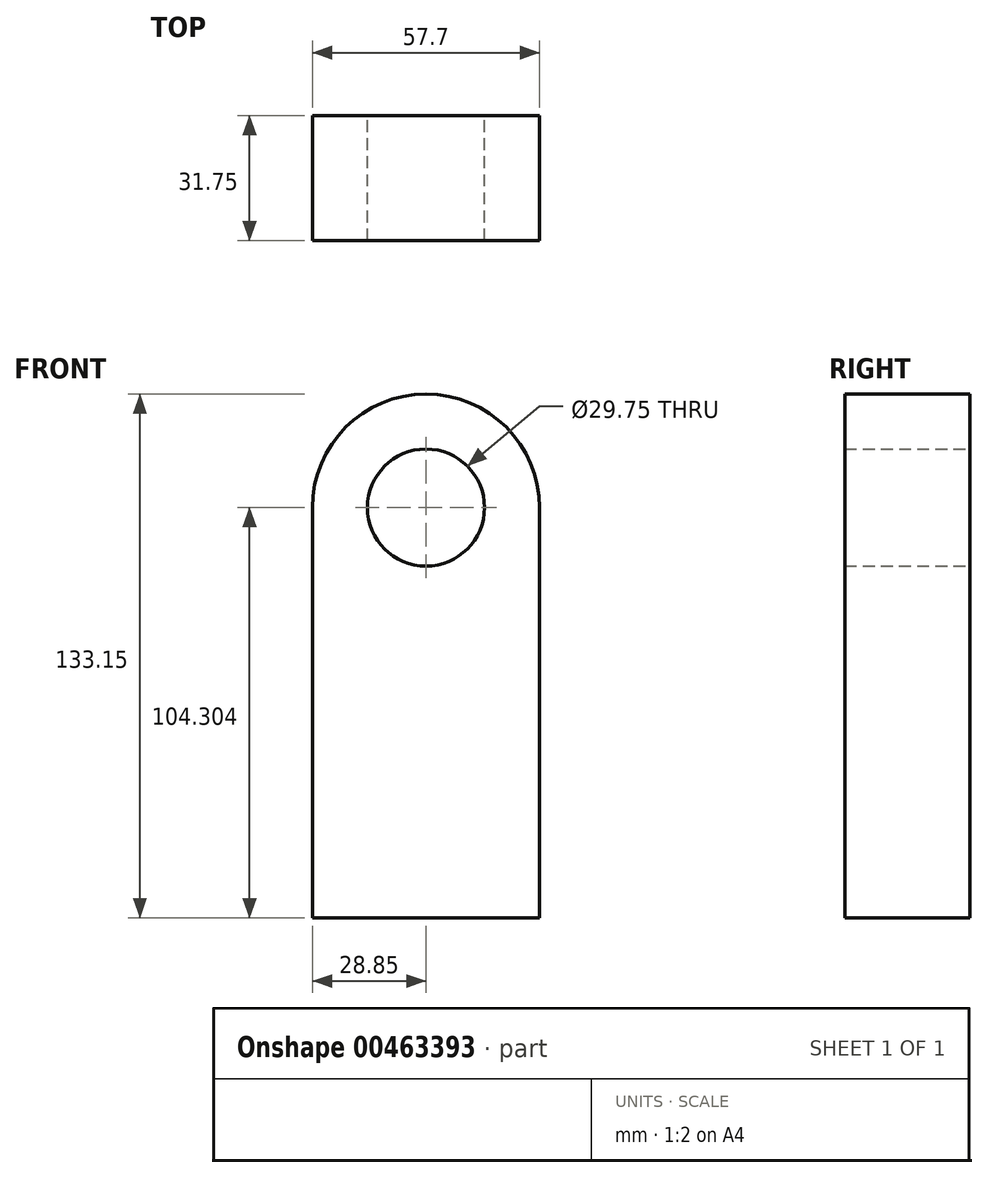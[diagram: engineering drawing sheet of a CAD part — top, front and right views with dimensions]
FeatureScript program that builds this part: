
annotation { "Feature Type Name" : "Feature", "Feature Type Description" : "" }
export const myFeature = defineFeature(function(context is Context, id is Id, definition is map)
    precondition{}
    {
        {
            var Q0;
            Q0=qCreatedBy(makeId("Front.planeOp"),FACE);
            var sketch = newSketch(context, id + "F0", { "sketchPlane" : qUnion([Q0])});
            skLineSegment(sketch, "E0.top", {"start": v(28.85, -52.15) * mm, "end": v(-28.85, -52.15) * mm});
            skLineSegment(sketch, "E0.left", {"start": v(28.85, 52.15) * mm, "end": v(28.85, -52.15) * mm});
            skLineSegment(sketch, "E0.right", {"start": v(-28.85, 52.15) * mm, "end": v(-28.85, -52.15) * mm});
            skPoint(sketch, "E0.middle", {"position": v(0, 0) * mm});
            skArc(sketch, "E1", {"start": v(28.85, 52.15) * mm, "mid": v(0, 81) * mm, "end": v(-28.85, 52.15) * mm});
            skCircle(sketch, "E2", {"center": v(0, 52.15) * mm, "radius": 14.88 * mm});
            skSolve(sketch);
        }
        {
            var Q0;
            Q0=makeQuery(id+"F0.imprint","IMPRINT",FACE,{"disambiguationData":[TD([[makeQuery(id+"F0.imprint","IMPRINT",EDGE,{"derivedFrom":sQuery(id+"F0.wireOp",EDGE,"E0.top")}),-1.0]])]});
            extrude(context, id + "F1", {"entities" : qUnion([Q0]), "depth" : 31.75 * mm});
        }
    });
